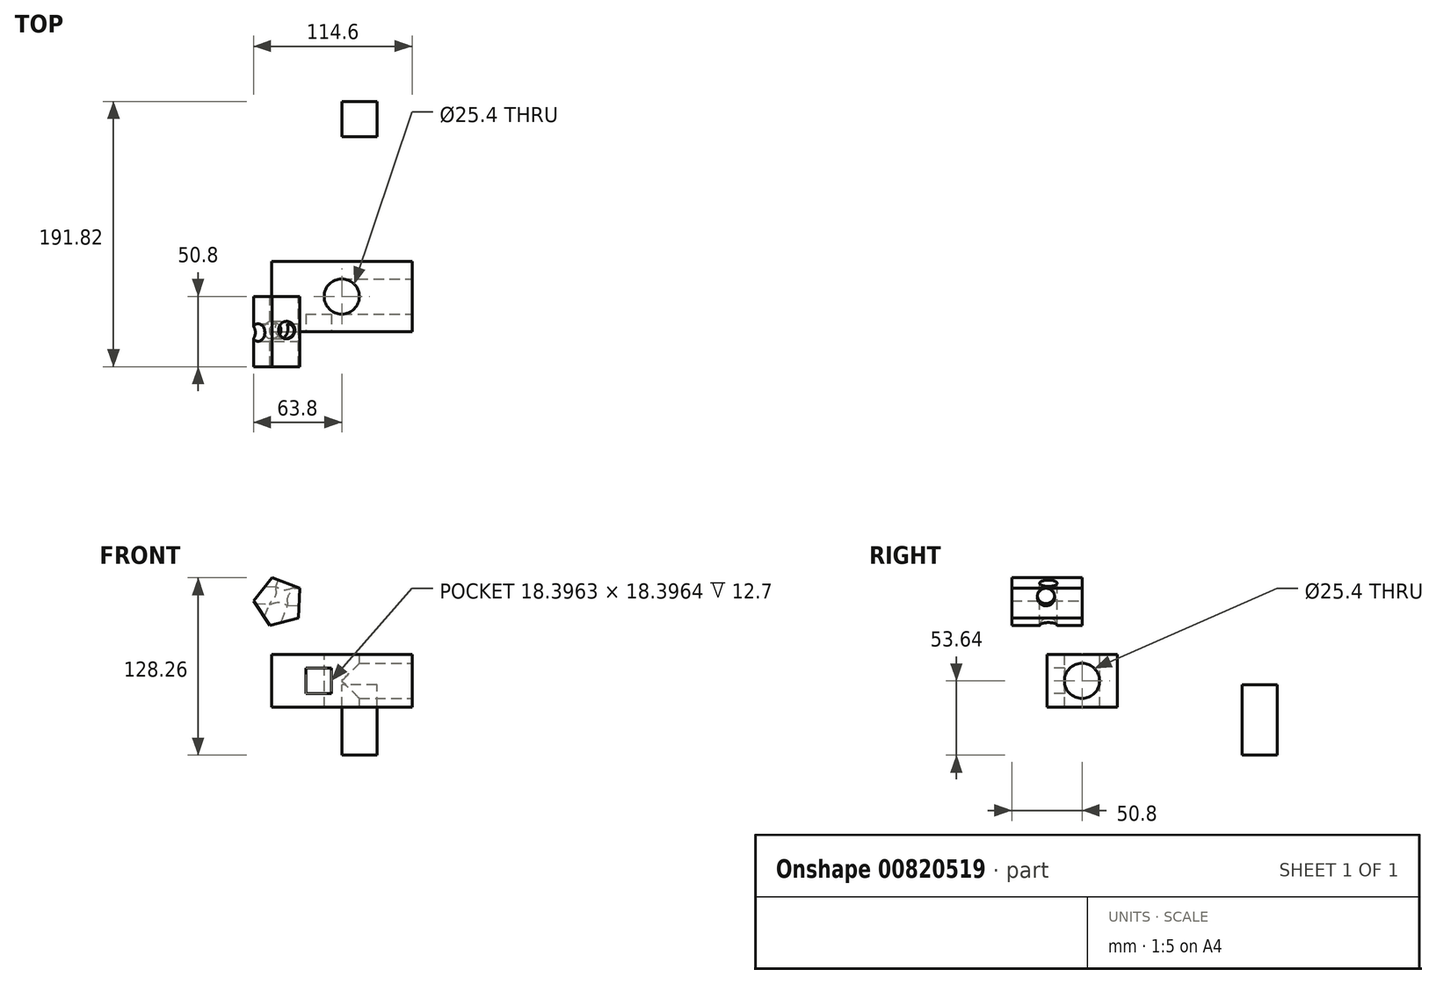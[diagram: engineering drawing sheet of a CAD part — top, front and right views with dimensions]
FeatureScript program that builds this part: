
annotation { "Feature Type Name" : "Feature", "Feature Type Description" : "" }
export const myFeature = defineFeature(function(context is Context, id is Id, definition is map)
    precondition{}
    {
        {
            var Q0;
            Q0=qCreatedBy(makeId("Top.planeOp"),FACE);
            var sketch = newSketch(context, id + "F0", { "sketchPlane" : qUnion([Q0])});
            skLineSegment(sketch, "E0.bottom", {"start": v(-50.8, 25.4) * mm, "end": v(50.8, 25.4) * mm});
            skLineSegment(sketch, "E0.top", {"start": v(-50.8, -25.4) * mm, "end": v(50.8, -25.4) * mm});
            skLineSegment(sketch, "E0.left", {"start": v(-50.8, 25.4) * mm, "end": v(-50.8, -25.4) * mm});
            skLineSegment(sketch, "E0.right", {"start": v(50.8, 25.4) * mm, "end": v(50.8, -25.4) * mm});
            skSolve(sketch);
        }
        {
            var Q0;
            Q0=makeQuery(id+"F0.imprint","IMPRINT",FACE,{"disambiguationData":[TD([[makeQuery(id+"F0.imprint","IMPRINT",EDGE,{"derivedFrom":sQuery(id+"F0.wireOp",EDGE,"E0.bottom")}),-1.0]])]});
            extrude(context, id + "F1", {"entities" : qUnion([Q0]), "endBound" : BoundingType.SYMMETRIC, "oppositeDirection" : true, "depth" : 38.1 * mm, "offsetDistance" : 25.4 * mm});
        }
        {
            var Q0;
            Q0=makeQuery(id+"F1.opExtrude","CAP_FACE",FACE,{"disambiguationData":[OSD([sQuery(id+"F0.wireOp",EDGE,"E0.bottom"),sQuery(id+"F0.wireOp",EDGE,"E0.top"),sQuery(id+"F0.wireOp",EDGE,"E0.left"),sQuery(id+"F0.wireOp",EDGE,"E0.right")])],"isStart":true});
            var sketch = newSketch(context, id + "F2", { "sketchPlane" : qUnion([Q0])});
            skCircle(sketch, "E1", {"center": v(0, 0) * mm, "radius": 12.7 * mm});
            skSolve(sketch);
        }
        {
            var Q0;
            Q0=makeQuery(id+"F2.imprint","IMPRINT",FACE,{"disambiguationData":[TD([[makeQuery(id+"F2.imprint","IMPRINT",EDGE,{"derivedFrom":sQuery(id+"F2.wireOp",EDGE,"E1")}),1.0]])]});
            extrude(context, id + "F3", {"entities" : qUnion([Q0]), "operationType" : NewBodyOperationType.REMOVE, "endBound" : BoundingType.THROUGH_ALL, "oppositeDirection" : true, "depth" : 38.1 * mm, "offsetDistance" : 25.4 * mm});
        }
        {
            var Q0;
            Q0=makeQuery(id+"F1.opExtrude","SWEPT_FACE",FACE,{"disambiguationData":[OSD([sQuery(id+"F0.wireOp",EDGE,"E0.right")])]});
            var sketch = newSketch(context, id + "F4", { "sketchPlane" : qUnion([Q0])});
            skCircle(sketch, "E2", {"center": v(0, 0) * mm, "radius": 12.7 * mm});
            skSolve(sketch);
        }
        {
            var Q0;
            Q0=makeQuery(id+"F4.imprint","IMPRINT",FACE,{"disambiguationData":[TD([[makeQuery(id+"F4.imprint","IMPRINT",EDGE,{"derivedFrom":sQuery(id+"F4.wireOp",EDGE,"E2")}),1.0]])]});
            extrude(context, id + "F5", {"entities" : qUnion([Q0]), "operationType" : NewBodyOperationType.REMOVE, "oppositeDirection" : true, "depth" : 50.8 * mm, "offsetDistance" : 25.4 * mm});
        }
        {
            var Q0;
            Q0=qCreatedBy(makeId("Front.planeOp"),FACE);
            var sketch = newSketch(context, id + "F6", { "sketchPlane" : qUnion([Q0])});
            skCircle(sketch, "E3.cCircle", {"center": v(-45.57, 57) * mm, "radius": 14.76 * mm, "construction": true});
            skLineSegment(sketch, "E3.0", {"start": v(-31.36, 45.56) * mm, "end": v(-52.07, 39.95) * mm});
            skLineSegment(sketch, "E3.1", {"start": v(-52.07, 39.95) * mm, "end": v(-63.8, 57.9) * mm});
            skLineSegment(sketch, "E3.2", {"start": v(-63.8, 57.9) * mm, "end": v(-50.34, 74.62) * mm});
            skLineSegment(sketch, "E3.3", {"start": v(-50.34, 74.62) * mm, "end": v(-30.3, 66.98) * mm});
            skLineSegment(sketch, "E3.4", {"start": v(-30.3, 66.98) * mm, "end": v(-31.36, 45.56) * mm});
            skPoint(sketch, "E3.0.midPoint", {"position": v(-41.71, 42.75) * mm});
            skSolve(sketch);
        }
        {
            var Q0;
            Q0=makeQuery(id+"F6.imprint","IMPRINT",FACE,{"disambiguationData":[TD([[makeQuery(id+"F6.imprint","IMPRINT",EDGE,{"derivedFrom":sQuery(id+"F6.wireOp",EDGE,"E3.0")}),-1.0]])]});
            extrude(context, id + "F7", {"entities" : qUnion([Q0]), "depth" : 50.8 * mm, "offsetDistance" : 25.4 * mm});
        }
        {
            var Q0;
            Q0=makeQuery(id+"F7.opExtrude","SWEPT_FACE",FACE,{"disambiguationData":[OSD([sQuery(id+"F6.wireOp",EDGE,"E3.3")])]});
            var sketch = newSketch(context, id + "F8", { "sketchPlane" : qUnion([Q0])});
            skCircle(sketch, "E4", {"center": v(-62.34, -24.29) * mm, "radius": 6.35 * mm});
            skSolve(sketch);
        }
        {
            var Q0;
            Q0=makeQuery(id+"F8.imprint","IMPRINT",FACE,{"disambiguationData":[TD([[makeQuery(id+"F8.imprint","IMPRINT",EDGE,{"derivedFrom":sQuery(id+"F8.wireOp",EDGE,"E4")}),1.0]])]});
            extrude(context, id + "F9", {"entities" : qUnion([Q0]), "operationType" : NewBodyOperationType.REMOVE, "endBound" : BoundingType.THROUGH_ALL, "oppositeDirection" : true, "depth" : 25.4 * mm, "offsetDistance" : 25.4 * mm});
        }
        {
            var Q0;
            Q0=makeQuery(id+"F7.opExtrude","SWEPT_FACE",FACE,{"disambiguationData":[OSD([sQuery(id+"F6.wireOp",EDGE,"E3.4")])]});
            var sketch = newSketch(context, id + "F10", { "sketchPlane" : qUnion([Q0])});
            skCircle(sketch, "E5", {"center": v(-26.05, 59.05) * mm, "radius": 6.35 * mm});
            skSolve(sketch);
        }
        {
            var Q0;
            Q0=makeQuery(id+"F10.imprint","IMPRINT",FACE,{"disambiguationData":[TD([[makeQuery(id+"F10.imprint","IMPRINT",EDGE,{"derivedFrom":sQuery(id+"F10.wireOp",EDGE,"E5")}),1.0]])]});
            extrude(context, id + "F11", {"entities" : qUnion([Q0]), "operationType" : NewBodyOperationType.REMOVE, "endBound" : BoundingType.THROUGH_ALL, "oppositeDirection" : true, "depth" : 25.4 * mm, "offsetDistance" : 25.4 * mm});
        }
        {
            var Q0;
            Q0=makeQuery(id+"F1.opExtrude","SWEPT_FACE",FACE,{"disambiguationData":[OSD([sQuery(id+"F0.wireOp",EDGE,"E0.top")])]});
            var sketch = newSketch(context, id + "F12", { "sketchPlane" : qUnion([Q0])});
            skCircle(sketch, "E6.cCircle", {"center": v(-16.77, 0) * mm, "radius": 9.2 * mm, "construction": true});
            skLineSegment(sketch, "E6.0", {"start": v(-7.57, 9.2) * mm, "end": v(-7.57, -9.2) * mm});
            skLineSegment(sketch, "E6.1", {"start": v(-7.57, -9.2) * mm, "end": v(-25.97, -9.2) * mm});
            skLineSegment(sketch, "E6.2", {"start": v(-25.97, -9.2) * mm, "end": v(-25.97, 9.2) * mm});
            skLineSegment(sketch, "E6.3", {"start": v(-25.97, 9.2) * mm, "end": v(-7.57, 9.2) * mm});
            skPoint(sketch, "E6.0.midPoint", {"position": v(-7.57, 0) * mm});
            skSolve(sketch);
        }
        {
            var Q0;
            Q0=makeQuery(id+"F12.imprint","IMPRINT",FACE,{"disambiguationData":[TD([[makeQuery(id+"F12.imprint","IMPRINT",EDGE,{"derivedFrom":sQuery(id+"F12.wireOp",EDGE,"E6.0")}),-1.0]])]});
            extrude(context, id + "F13", {"entities" : qUnion([Q0]), "operationType" : NewBodyOperationType.REMOVE, "oppositeDirection" : true, "depth" : 12.7 * mm, "offsetDistance" : 25.4 * mm});
        }
        {
            var Q0;
            Q0=qCreatedBy(makeId("Right.planeOp"),FACE);
            var sketch = newSketch(context, id + "F14", { "sketchPlane" : qUnion([Q0])});
            skLineSegment(sketch, "E7.bottom", {"start": v(141.02, -53.64) * mm, "end": v(115.62, -53.64) * mm});
            skLineSegment(sketch, "E7.top", {"start": v(141.02, -2.84) * mm, "end": v(115.62, -2.84) * mm});
            skLineSegment(sketch, "E7.left", {"start": v(141.02, -53.64) * mm, "end": v(141.02, -2.84) * mm});
            skLineSegment(sketch, "E7.right", {"start": v(115.62, -53.64) * mm, "end": v(115.62, -2.84) * mm});
            skSolve(sketch);
        }
        {
            var Q0;
            Q0=makeQuery(id+"F14.imprint","IMPRINT",FACE,{"disambiguationData":[TD([[makeQuery(id+"F14.imprint","IMPRINT",EDGE,{"derivedFrom":sQuery(id+"F14.wireOp",EDGE,"E7.bottom")}),-1.0]])]});
            extrude(context, id + "F15", {"entities" : qUnion([Q0]), "depth" : 25.4 * mm, "offsetDistance" : 25.4 * mm});
        }
    });
